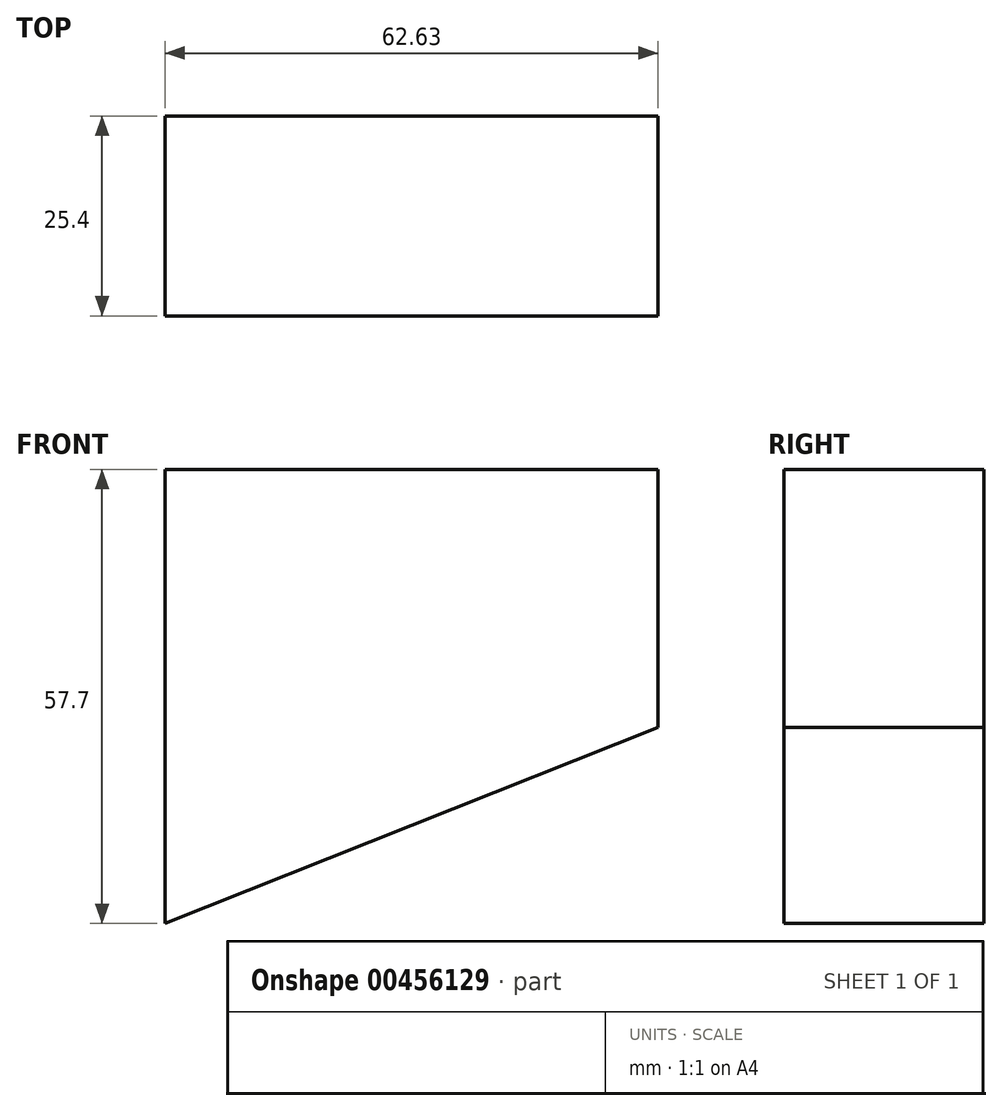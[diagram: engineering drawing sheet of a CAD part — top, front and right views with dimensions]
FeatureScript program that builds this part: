
annotation { "Feature Type Name" : "Feature", "Feature Type Description" : "" }
export const myFeature = defineFeature(function(context is Context, id is Id, definition is map)
    precondition{}
    {
        {
            var Q0;
            Q0=qCreatedBy(makeId("Front.planeOp"),FACE);
            var sketch = newSketch(context, id + "F0", { "sketchPlane" : qUnion([Q0])});
            skLineSegment(sketch, "E0", {"start": v(0, 0) * mm, "end": v(62.63, 0) * mm});
            skLineSegment(sketch, "E1", {"start": v(62.63, 0) * mm, "end": v(62.63, -32.75) * mm});
            skLineSegment(sketch, "E2", {"start": v(62.63, -32.75) * mm, "end": v(0, -57.7) * mm});
            skLineSegment(sketch, "E3", {"start": v(0, -57.7) * mm, "end": v(0, 0) * mm});
            skSolve(sketch);
        }
        {
            var Q0;
            Q0=makeQuery(id+"F0.imprint","IMPRINT",FACE,{"disambiguationData":[TD([[makeQuery(id+"F0.imprint","IMPRINT",EDGE,{"derivedFrom":sQuery(id+"F0.wireOp",EDGE,"E0")}),-1.0]])]});
            extrude(context, id + "F1", {"entities" : qUnion([Q0]), "depth" : 25.4 * mm});
        }
    });
